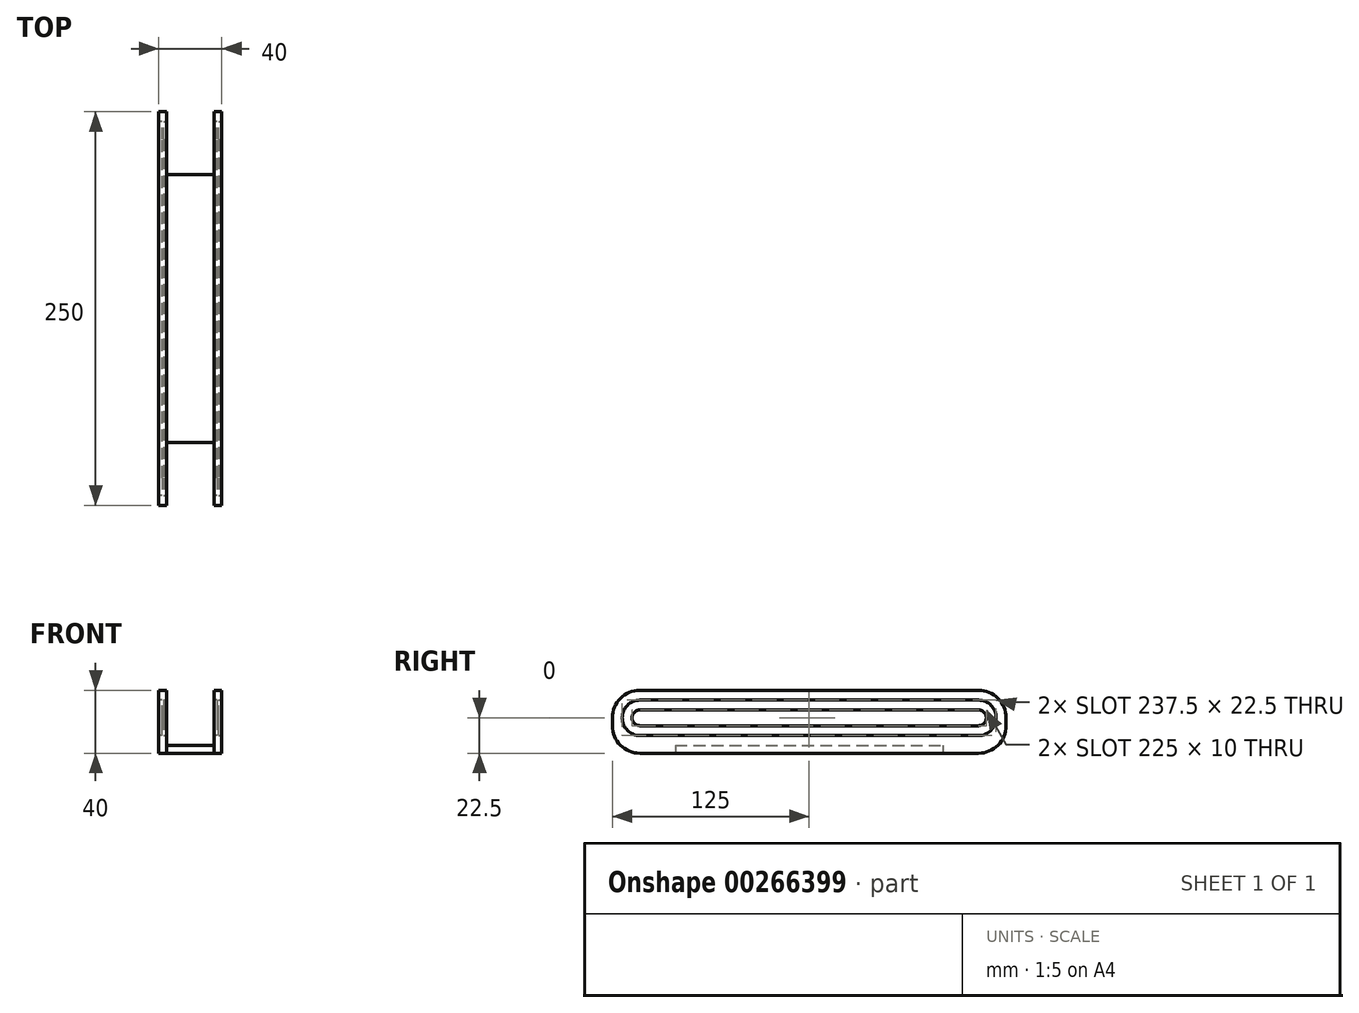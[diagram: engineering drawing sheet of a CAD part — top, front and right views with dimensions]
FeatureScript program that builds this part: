
annotation { "Feature Type Name" : "Feature", "Feature Type Description" : "" }
export const myFeature = defineFeature(function(context is Context, id is Id, definition is map)
    precondition{}
    {
        {
            var Q0;
            Q0=qCreatedBy(makeId("Front.planeOp"),FACE);
            var sketch = newSketch(context, id + "F0", { "sketchPlane" : qUnion([Q0])});
            skLineSegment(sketch, "E0.bottom", {"start": v(20, -20) * mm, "end": v(-20, -20) * mm});
            skLineSegment(sketch, "E0.left", {"start": v(20, -20) * mm, "end": v(20, 20) * mm});
            skLineSegment(sketch, "E0.right", {"start": v(-20, -20) * mm, "end": v(-20, 20) * mm});
            skPoint(sketch, "E0.middle", {"position": v(0, 0) * mm});
            skLineSegment(sketch, "E1", {"start": v(-20, 20) * mm, "end": v(-15, 20) * mm});
            skLineSegment(sketch, "E2", {"start": v(20, 20) * mm, "end": v(15, 20) * mm});
            skLineSegment(sketch, "E3", {"start": v(-15, 20) * mm, "end": v(-15, -15) * mm});
            skLineSegment(sketch, "E4", {"start": v(-15, -15) * mm, "end": v(15, -15) * mm});
            skLineSegment(sketch, "E5", {"start": v(15, -15) * mm, "end": v(15, 20) * mm});
            skSolve(sketch);
        }
        {
            var Q0;
            Q0=makeQuery(id+"F0.imprint","IMPRINT",FACE,{"disambiguationData":[TD([[makeQuery(id+"F0.imprint","IMPRINT",EDGE,{"derivedFrom":sQuery(id+"F0.wireOp",EDGE,"E0.bottom")}),-1.0]])]});
            extrude(context, id + "F1", {"entities" : qUnion([Q0]), "depth" : 125 * mm, "hasSecondDirection" : true, "secondDirectionOppositeDirection" : true, "secondDirectionDepth" : 125 * mm});
        }
        {
            var Q0;
            Q0=makeQuery(id+"F1.opExtrude","SWEPT_FACE",FACE,{"disambiguationData":[OSD([sQuery(id+"F0.wireOp",EDGE,"E3")])]});
            var sketch = newSketch(context, id + "F2", { "sketchPlane" : qUnion([Q0])});
            skPoint(sketch, "E6.endSnap0", {"position": v(0, 2.5) * mm});
            skLineSegment(sketch, "E7", {"start": v(0, 13.75) * mm, "end": v(-107.5, 13.75) * mm});
            skLineSegment(sketch, "E8", {"start": v(0, 7.5) * mm, "end": v(-107.5, 7.5) * mm});
            skLineSegment(sketch, "E9", {"start": v(0, -8.75) * mm, "end": v(-107.5, -8.75) * mm});
            skLineSegment(sketch, "E10", {"start": v(0, -2.5) * mm, "end": v(-107.5, -2.5) * mm});
            skArc(sketch, "E11", {"start": v(-107.5, 13.75) * mm, "mid": v(-118.75, 2.5) * mm, "end": v(-107.5, -8.75) * mm});
            skArc(sketch, "E12", {"start": v(-107.5, 7.5) * mm, "mid": v(-112.5, 2.5) * mm, "end": v(-107.5, -2.5) * mm});
            skLineSegment(sketch, "E13", {"start": v(0, 13.75) * mm, "end": v(107.5, 13.75) * mm});
            skLineSegment(sketch, "E14", {"start": v(0, -8.75) * mm, "end": v(107.5, -8.75) * mm});
            skLineSegment(sketch, "E15", {"start": v(0, -2.5) * mm, "end": v(107.5, -2.5) * mm});
            skLineSegment(sketch, "E16", {"start": v(0, 7.5) * mm, "end": v(107.5, 7.5) * mm});
            skArc(sketch, "E17", {"start": v(107.5, -8.75) * mm, "mid": v(118.75, 2.5) * mm, "end": v(107.5, 13.75) * mm});
            skArc(sketch, "E18", {"start": v(107.5, -2.5) * mm, "mid": v(112.5, 2.5) * mm, "end": v(107.5, 7.5) * mm});
            skPoint(sketch, "E19.orphan", {"position": v(-125, 2.5) * mm});
            skPoint(sketch, "E20.orphan", {"position": v(-118.75, 2.5) * mm});
            skPoint(sketch, "E21.orphan", {"position": v(118.75, 2.5) * mm});
            skPoint(sketch, "E22.trimOffspring.end.orphan", {"position": v(125, 2.5) * mm});
            skSolve(sketch);
        }
        {
            var Q0;
            Q0=makeQuery(id+"F1.opExtrude","SWEPT_FACE",FACE,{"disambiguationData":[OSD([sQuery(id+"F0.wireOp",EDGE,"E5")])]});
            var sketch = newSketch(context, id + "F3", { "sketchPlane" : qUnion([Q0])});
            skPoint(sketch, "E23.endSnap0", {"position": v(0, 20) * mm});
            skPoint(sketch, "E24.endSnap0", {"position": v(0, -15) * mm});
            skLineSegment(sketch, "E25", {"start": v(0, 7.5) * mm, "end": v(-107.5, 7.5) * mm});
            skLineSegment(sketch, "E26", {"start": v(0, -2.5) * mm, "end": v(-107.5, -2.5) * mm});
            skLineSegment(sketch, "E27", {"start": v(0, 7.5) * mm, "end": v(107.5, 7.5) * mm});
            skLineSegment(sketch, "E28", {"start": v(0, -2.5) * mm, "end": v(107.5, -2.5) * mm});
            skLineSegment(sketch, "E29", {"start": v(0, 13.75) * mm, "end": v(107.5, 13.75) * mm});
            skLineSegment(sketch, "E30", {"start": v(0, -8.75) * mm, "end": v(107.5, -8.75) * mm});
            skLineSegment(sketch, "E31", {"start": v(0, 13.75) * mm, "end": v(-107.5, 13.75) * mm});
            skLineSegment(sketch, "E32", {"start": v(0, -8.75) * mm, "end": v(-107.5, -8.75) * mm});
            skPoint(sketch, "E33.end.orphan", {"position": v(-125, 2.5) * mm});
            skArc(sketch, "E34", {"start": v(-107.5, 7.5) * mm, "mid": v(-112.5, 2.5) * mm, "end": v(-107.5, -2.5) * mm});
            skArc(sketch, "E35", {"start": v(-107.5, 13.75) * mm, "mid": v(-118.75, 2.5) * mm, "end": v(-107.5, -8.75) * mm});
            skPoint(sketch, "E36.end.orphan", {"position": v(125, 2.5) * mm});
            skPoint(sketch, "E36.start.orphan", {"position": v(0, 2.5) * mm});
            skArc(sketch, "E37", {"start": v(107.5, -2.5) * mm, "mid": v(112.5, 2.5) * mm, "end": v(107.5, 7.5) * mm});
            skArc(sketch, "E38", {"start": v(107.5, -8.75) * mm, "mid": v(118.75, 2.5) * mm, "end": v(107.5, 13.75) * mm});
            skPoint(sketch, "E24.start.orphan", {"position": v(0, -15) * mm});
            skSolve(sketch);
        }
        {
            var Q0;
            Q0=makeQuery(id+"F1.opExtrude","SWEPT_FACE",FACE,{"disambiguationData":[OSD([sQuery(id+"F0.wireOp",EDGE,"E0.right")])]});
            var sketch = newSketch(context, id + "F4", { "sketchPlane" : qUnion([Q0])});
            skPoint(sketch, "E39.endSnap0", {"position": v(0, 20) * mm});
            skLineSegment(sketch, "E40", {"start": v(0, 13.75) * mm, "end": v(-107.5, 13.75) * mm});
            skLineSegment(sketch, "E41", {"start": v(0, -8.75) * mm, "end": v(-107.5, -8.75) * mm});
            skLineSegment(sketch, "E42", {"start": v(0, 7.5) * mm, "end": v(-107.5, 7.5) * mm});
            skLineSegment(sketch, "E43", {"start": v(0, -2.5) * mm, "end": v(-107.5, -2.5) * mm});
            skLineSegment(sketch, "E44", {"start": v(0, 13.75) * mm, "end": v(107.5, 13.75) * mm});
            skLineSegment(sketch, "E45", {"start": v(0, 7.5) * mm, "end": v(107.5, 7.5) * mm});
            skLineSegment(sketch, "E46", {"start": v(0, -2.5) * mm, "end": v(107.5, -2.5) * mm});
            skLineSegment(sketch, "E47", {"start": v(0, -8.75) * mm, "end": v(107.5, -8.75) * mm});
            skArc(sketch, "E48", {"start": v(107.5, -2.5) * mm, "mid": v(112.5, 2.5) * mm, "end": v(107.5, 7.5) * mm});
            skArc(sketch, "E49", {"start": v(107.5, -8.75) * mm, "mid": v(118.75, 2.5) * mm, "end": v(107.5, 13.75) * mm});
            skArc(sketch, "E50", {"start": v(-107.5, 7.5) * mm, "mid": v(-112.5, 2.5) * mm, "end": v(-107.5, -2.5) * mm});
            skArc(sketch, "E51", {"start": v(-107.5, 13.75) * mm, "mid": v(-118.75, 2.5) * mm, "end": v(-107.5, -8.75) * mm});
            skPoint(sketch, "E52.orphan", {"position": v(-125, 2.5) * mm});
            skPoint(sketch, "E53.orphan", {"position": v(-125, -2.5) * mm});
            skPoint(sketch, "E54.start.orphan", {"position": v(-125, 7.5) * mm});
            skPoint(sketch, "E55.orphan", {"position": v(125, 2.5) * mm});
            skPoint(sketch, "E56.end.orphan", {"position": v(125, -2.5) * mm});
            skPoint(sketch, "E57.orphan", {"position": v(125, 7.5) * mm});
            skSolve(sketch);
        }
        {
            var Q0;
            Q0=makeQuery(id+"F1.opExtrude","SWEPT_FACE",FACE,{"disambiguationData":[OSD([sQuery(id+"F0.wireOp",EDGE,"E0.left")])]});
            var sketch = newSketch(context, id + "F5", { "sketchPlane" : qUnion([Q0])});
            skLineSegment(sketch, "E58", {"start": v(0, 13.75) * mm, "end": v(-107.5, 13.75) * mm});
            skLineSegment(sketch, "E59", {"start": v(0, -8.75) * mm, "end": v(-107.5, -8.75) * mm});
            skLineSegment(sketch, "E60", {"start": v(0, 13.75) * mm, "end": v(107.5, 13.75) * mm});
            skLineSegment(sketch, "E61", {"start": v(0, -8.75) * mm, "end": v(107.5, -8.75) * mm});
            skLineSegment(sketch, "E62", {"start": v(0, 7.5) * mm, "end": v(107.5, 7.5) * mm});
            skLineSegment(sketch, "E63", {"start": v(0, -2.5) * mm, "end": v(107.5, -2.5) * mm});
            skLineSegment(sketch, "E64", {"start": v(0, 7.5) * mm, "end": v(-107.5, 7.5) * mm});
            skLineSegment(sketch, "E65", {"start": v(0, -2.5) * mm, "end": v(-107.5, -2.5) * mm});
            skArc(sketch, "E66", {"start": v(107.5, -2.5) * mm, "mid": v(112.5, 2.5) * mm, "end": v(107.5, 7.5) * mm});
            skArc(sketch, "E67", {"start": v(107.5, -8.75) * mm, "mid": v(118.75, 2.5) * mm, "end": v(107.5, 13.75) * mm});
            skArc(sketch, "E68", {"start": v(-107.5, 7.5) * mm, "mid": v(-112.5, 2.5) * mm, "end": v(-107.5, -2.5) * mm});
            skArc(sketch, "E69", {"start": v(-107.5, 13.75) * mm, "mid": v(-118.75, 2.5) * mm, "end": v(-107.5, -8.75) * mm});
            skPoint(sketch, "E70.orphan", {"position": v(-125, 7.5) * mm});
            skPoint(sketch, "E71.start.orphan", {"position": v(-125, 2.5) * mm});
            skPoint(sketch, "E72.orphan", {"position": v(-125, -2.5) * mm});
            skPoint(sketch, "E73.start.orphan", {"position": v(0, 20) * mm});
            skPoint(sketch, "E74.start.orphan", {"position": v(125, 2.5) * mm});
            skPoint(sketch, "E75.orphan", {"position": v(125, 7.5) * mm});
            skPoint(sketch, "E76.end.orphan", {"position": v(125, -2.5) * mm});
            skSolve(sketch);
        }
        {
            var Q0;
            Q0=makeQuery(id+"F3.imprint","IMPRINT",FACE,{"disambiguationData":[TD([[makeQuery(id+"F3.imprint","IMPRINT",EDGE,{"derivedFrom":sQuery(id+"F3.wireOp",EDGE,"E25")}),1.0]])]});
            extrude(context, id + "F6", {"entities" : qUnion([Q0]), "operationType" : NewBodyOperationType.REMOVE, "endBound" : BoundingType.THROUGH_ALL, "oppositeDirection" : true, "depth" : 25 * mm});
        }
        {
            var Q0;
            Q0=makeQuery(id+"F2.imprint","IMPRINT",FACE,{"disambiguationData":[TD([[makeQuery(id+"F2.imprint","IMPRINT",EDGE,{"derivedFrom":sQuery(id+"F2.wireOp",EDGE,"E8")}),1.0]])]});
            extrude(context, id + "F7", {"entities" : qUnion([Q0]), "operationType" : NewBodyOperationType.REMOVE, "endBound" : BoundingType.THROUGH_ALL, "oppositeDirection" : true, "depth" : 25 * mm});
        }
        {
            var Q0;
            Q0=makeQuery(id+"F3.imprint","IMPRINT",FACE,{"disambiguationData":[TD([[makeQuery(id+"F3.imprint","IMPRINT",EDGE,{"derivedFrom":sQuery(id+"F3.wireOp",EDGE,"E25")}),-1.0]])]});
            extrude(context, id + "F8", {"entities" : qUnion([Q0]), "operationType" : NewBodyOperationType.REMOVE, "oppositeDirection" : true, "depth" : 2 * mm});
        }
        {
            var Q0;
            Q0=makeQuery(id+"F2.imprint","IMPRINT",FACE,{"disambiguationData":[TD([[makeQuery(id+"F2.imprint","IMPRINT",EDGE,{"derivedFrom":sQuery(id+"F2.wireOp",EDGE,"E7")}),1.0]])]});
            extrude(context, id + "F9", {"entities" : qUnion([Q0]), "operationType" : NewBodyOperationType.REMOVE, "oppositeDirection" : true, "depth" : 2 * mm});
        }
        {
            var Q0;
            Q0=makeQuery(id+"F4.imprint","IMPRINT",FACE,{"disambiguationData":[TD([[makeQuery(id+"F4.imprint","IMPRINT",EDGE,{"derivedFrom":sQuery(id+"F4.wireOp",EDGE,"E40")}),1.0]])]});
            extrude(context, id + "F10", {"entities" : qUnion([Q0]), "operationType" : NewBodyOperationType.REMOVE, "oppositeDirection" : true, "depth" : 2 * mm});
        }
        {
            var Q0;
            Q0=makeQuery(id+"F5.imprint","IMPRINT",FACE,{"disambiguationData":[TD([[makeQuery(id+"F5.imprint","IMPRINT",EDGE,{"derivedFrom":sQuery(id+"F5.wireOp",EDGE,"E58")}),1.0]])]});
            extrude(context, id + "F11", {"entities" : qUnion([Q0]), "operationType" : NewBodyOperationType.REMOVE, "oppositeDirection" : true, "depth" : 2 * mm});
        }
        {
            var Q0;
            Q0=makeQuery(id+"F1.opExtrude","SWEPT_FACE",FACE,{"disambiguationData":[OSD([sQuery(id+"F0.wireOp",EDGE,"E0.bottom")])]});
            var sketch = newSketch(context, id + "F12", { "sketchPlane" : qUnion([Q0])});
            skLineSegment(sketch, "E77", {"start": v(-15, 125) * mm, "end": v(15, 125) * mm});
            skLineSegment(sketch, "E78", {"start": v(-15, 125) * mm, "end": v(-15, 85) * mm});
            skLineSegment(sketch, "E79", {"start": v(-15, 85) * mm, "end": v(15, 85) * mm});
            skLineSegment(sketch, "E80", {"start": v(15, 85) * mm, "end": v(15, 125) * mm});
            skLineSegment(sketch, "E81", {"start": v(-15, -125) * mm, "end": v(15, -125) * mm});
            skLineSegment(sketch, "E82", {"start": v(-15, -125) * mm, "end": v(-15, -85) * mm});
            skLineSegment(sketch, "E83", {"start": v(-15, -85) * mm, "end": v(15, -85) * mm});
            skLineSegment(sketch, "E84", {"start": v(15, -85) * mm, "end": v(15, -125) * mm});
            skSolve(sketch);
        }
        {
            var Q0;
            Q0=makeQuery(id+"F12.imprint","IMPRINT",FACE,{"disambiguationData":[TD([[makeQuery(id+"F12.imprint","IMPRINT",EDGE,{"derivedFrom":sQuery(id+"F12.wireOp",EDGE,"E81")}),-1.0]])]});
            var Q1;
            Q1=makeQuery(id+"F12.imprint","IMPRINT",FACE,{"disambiguationData":[TD([[makeQuery(id+"F12.imprint","IMPRINT",EDGE,{"derivedFrom":sQuery(id+"F12.wireOp",EDGE,"E77")}),1.0]])]});
            extrude(context, id + "F13", {"entities" : qUnion([Q0, Q1]), "operationType" : NewBodyOperationType.REMOVE, "endBound" : BoundingType.THROUGH_ALL, "oppositeDirection" : true, "depth" : 25 * mm});
        }
        {
            var Q0;
            {var subQ1=sQuery(id+"F0.wireOp",EDGE,"E0.right");var subQ2=sQuery(id+"F0.wireOp",EDGE,"E0.bottom");Q0=makeQuery(id+"F13.boolean.opBoolean","SPLIT",EDGE,{"disambiguationData":[TD([makeQuery(id+"F1.opExtrude","SWEPT_FACE",FACE,{"disambiguationData":[OSD([subQ1])]})])],"derivedFrom":makeQuery(id+"F1.opExtrude","CAP_EDGE",EDGE,{"disambiguationData":[OSD([subQ2])],"isStart":true})});}
            var Q1;
            Q1=makeQuery(id+"F1.opExtrude","CAP_EDGE",EDGE,{"disambiguationData":[OSD([sQuery(id+"F0.wireOp",EDGE,"E1")])],"isStart":true});
            var Q2;
            Q2=makeQuery(id+"F1.opExtrude","CAP_EDGE",EDGE,{"disambiguationData":[OSD([sQuery(id+"F0.wireOp",EDGE,"E2")])],"isStart":true});
            var Q3;
            {var subQ1=sQuery(id+"F0.wireOp",EDGE,"E0.left");var subQ2=sQuery(id+"F0.wireOp",EDGE,"E0.bottom");Q3=makeQuery(id+"F13.boolean.opBoolean","SPLIT",EDGE,{"disambiguationData":[TD([makeQuery(id+"F1.opExtrude","SWEPT_FACE",FACE,{"disambiguationData":[OSD([subQ1])]})])],"derivedFrom":makeQuery(id+"F1.opExtrude","CAP_EDGE",EDGE,{"disambiguationData":[OSD([subQ2])],"isStart":true})});}
            var Q4;
            {var subQ1=sQuery(id+"F0.wireOp",EDGE,"E0.left");var subQ2=sQuery(id+"F0.wireOp",EDGE,"E0.bottom");Q4=makeQuery(id+"F13.boolean.opBoolean","SPLIT",EDGE,{"disambiguationData":[TD([makeQuery(id+"F1.opExtrude","SWEPT_FACE",FACE,{"disambiguationData":[OSD([subQ1])]})])],"derivedFrom":makeQuery(id+"F1.opExtrude","CAP_EDGE",EDGE,{"disambiguationData":[OSD([subQ2])],"isStart":false})});}
            var Q5;
            Q5=makeQuery(id+"F1.opExtrude","CAP_EDGE",EDGE,{"disambiguationData":[OSD([sQuery(id+"F0.wireOp",EDGE,"E2")])],"isStart":false});
            var Q6;
            {var subQ0=sQuery(id+"F0.wireOp",EDGE,"E0.right");var subQ2=sQuery(id+"F0.wireOp",EDGE,"E0.bottom");Q6=makeQuery(id+"F13.boolean.opBoolean","SPLIT",EDGE,{"disambiguationData":[TD([makeQuery(id+"F1.opExtrude","SWEPT_FACE",FACE,{"disambiguationData":[OSD([subQ0])]})])],"derivedFrom":makeQuery(id+"F1.opExtrude","CAP_EDGE",EDGE,{"disambiguationData":[OSD([subQ2])],"isStart":false})});}
            var Q7;
            Q7=makeQuery(id+"F1.opExtrude","CAP_EDGE",EDGE,{"disambiguationData":[OSD([sQuery(id+"F0.wireOp",EDGE,"E1")])],"isStart":false});
            fillet(context, id + "F14", {"entities" : qUnion([Q0, Q1, Q2, Q3, Q4, Q5, Q6, Q7]), "radius" : 17.5 * mm, "tangentPropagation" : true, "allowEdgeOverflow" : false});
        }
    });
